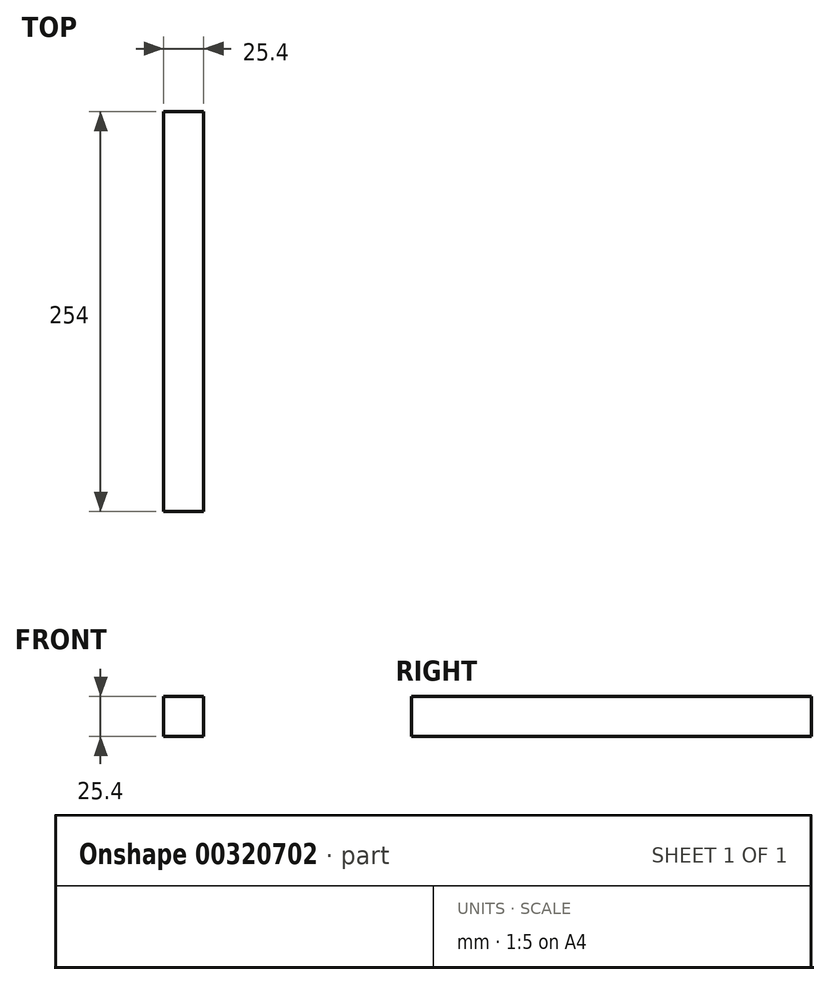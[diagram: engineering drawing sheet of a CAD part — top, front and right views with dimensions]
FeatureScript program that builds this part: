
annotation { "Feature Type Name" : "Feature", "Feature Type Description" : "" }
export const myFeature = defineFeature(function(context is Context, id is Id, definition is map)
    precondition{}
    {
        {
            var Q0;
            Q0=qCreatedBy(makeId("Top.planeOp"),FACE);
            var sketch = newSketch(context, id + "F0", { "sketchPlane" : qUnion([Q0])});
            skLineSegment(sketch, "E0", {"start": v(-156.7, 222.18) * mm, "end": v(-156.7, -31.82) * mm});
            skLineSegment(sketch, "E1", {"start": v(-156.7, -31.82) * mm, "end": v(-131.3, -31.82) * mm});
            skLineSegment(sketch, "E2", {"start": v(-131.3, -31.82) * mm, "end": v(-131.3, 222.18) * mm});
            skLineSegment(sketch, "E3", {"start": v(-131.3, 222.18) * mm, "end": v(-156.7, 222.18) * mm});
            skSolve(sketch);
        }
        {
            var Q0;
            Q0=qSketchRegion(id+"F0",true);
            extrude(context, id + "F1", {"entities" : qUnion([Q0]), "depth" : 25.4 * mm});
        }
    });
